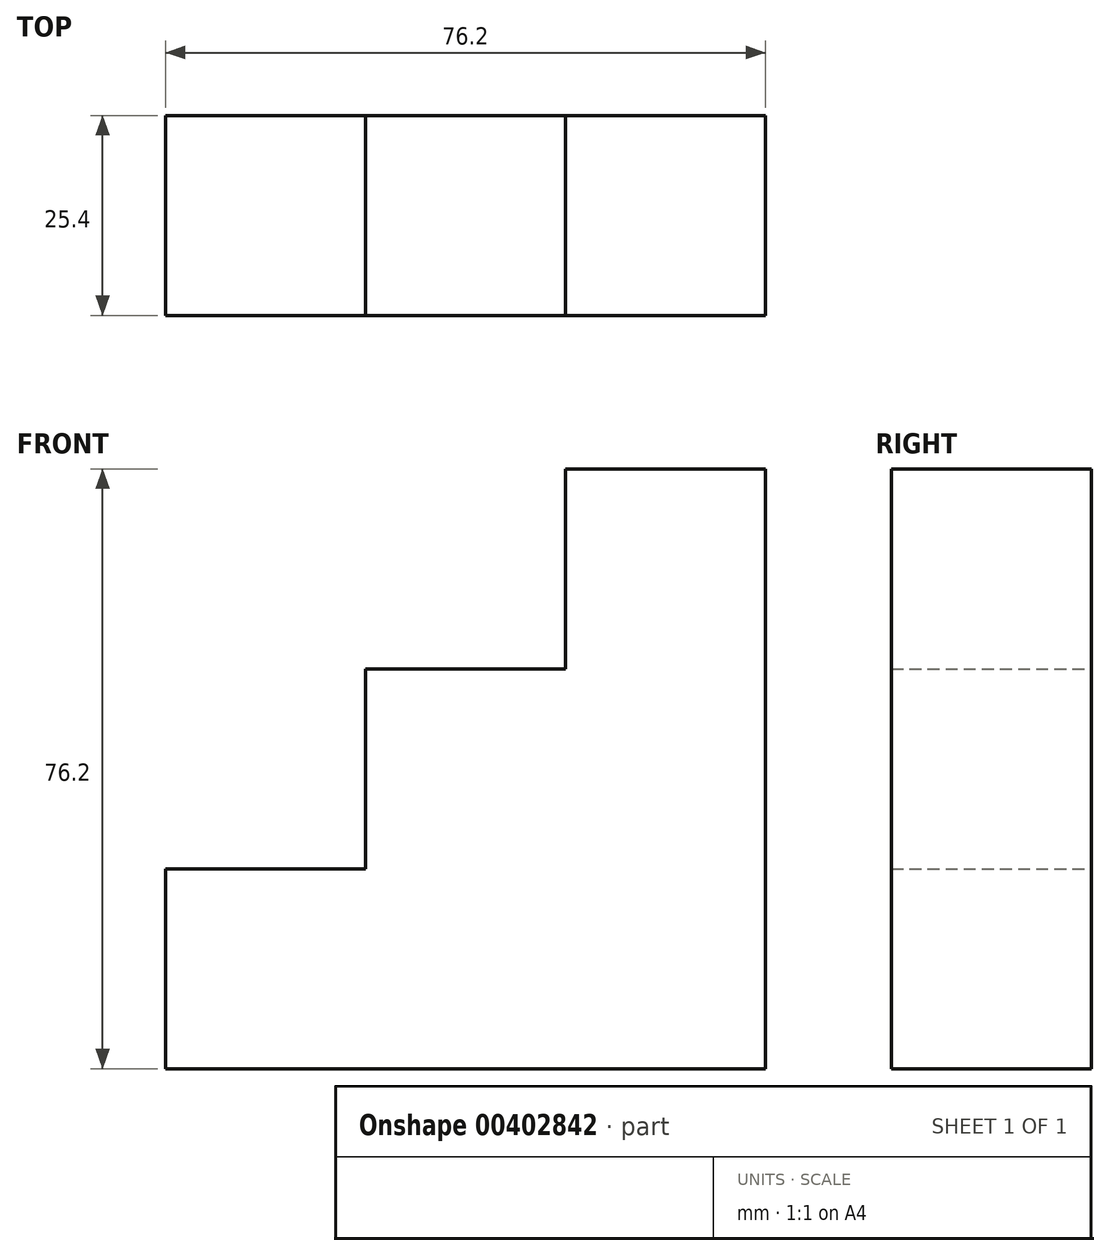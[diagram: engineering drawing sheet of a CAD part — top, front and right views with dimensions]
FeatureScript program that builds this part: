
annotation { "Feature Type Name" : "Feature", "Feature Type Description" : "" }
export const myFeature = defineFeature(function(context is Context, id is Id, definition is map)
    precondition{}
    {
        {
            var Q0;
            Q0=qCreatedBy(makeId("Front.planeOp"),FACE);
            var sketch = newSketch(context, id + "F0", { "sketchPlane" : qUnion([Q0])});
            skLineSegment(sketch, "E0", {"start": v(-52.94, -50.8) * mm, "end": v(23.26, -50.8) * mm});
            skLineSegment(sketch, "E1", {"start": v(23.26, -50.8) * mm, "end": v(23.26, 25.4) * mm});
            skLineSegment(sketch, "E2", {"start": v(23.26, 25.4) * mm, "end": v(-2.14, 25.4) * mm});
            skLineSegment(sketch, "E3", {"start": v(-2.14, 25.4) * mm, "end": v(-2.14, 0) * mm});
            skLineSegment(sketch, "E4", {"start": v(-2.14, 0) * mm, "end": v(-27.54, 0) * mm});
            skLineSegment(sketch, "E5", {"start": v(-27.54, 0) * mm, "end": v(-27.54, -25.4) * mm});
            skLineSegment(sketch, "E6", {"start": v(-27.54, -25.4) * mm, "end": v(-52.94, -25.4) * mm});
            skLineSegment(sketch, "E7", {"start": v(-52.94, -25.4) * mm, "end": v(-52.94, -50.8) * mm});
            skSolve(sketch);
        }
        {
            var Q0;
            Q0 = qSketchRegion(id + "F0", true);
            extrude(context, id + "F1", {"entities" : qUnion([Q0]), "depth" : 25.4 * mm});
        }
    });
